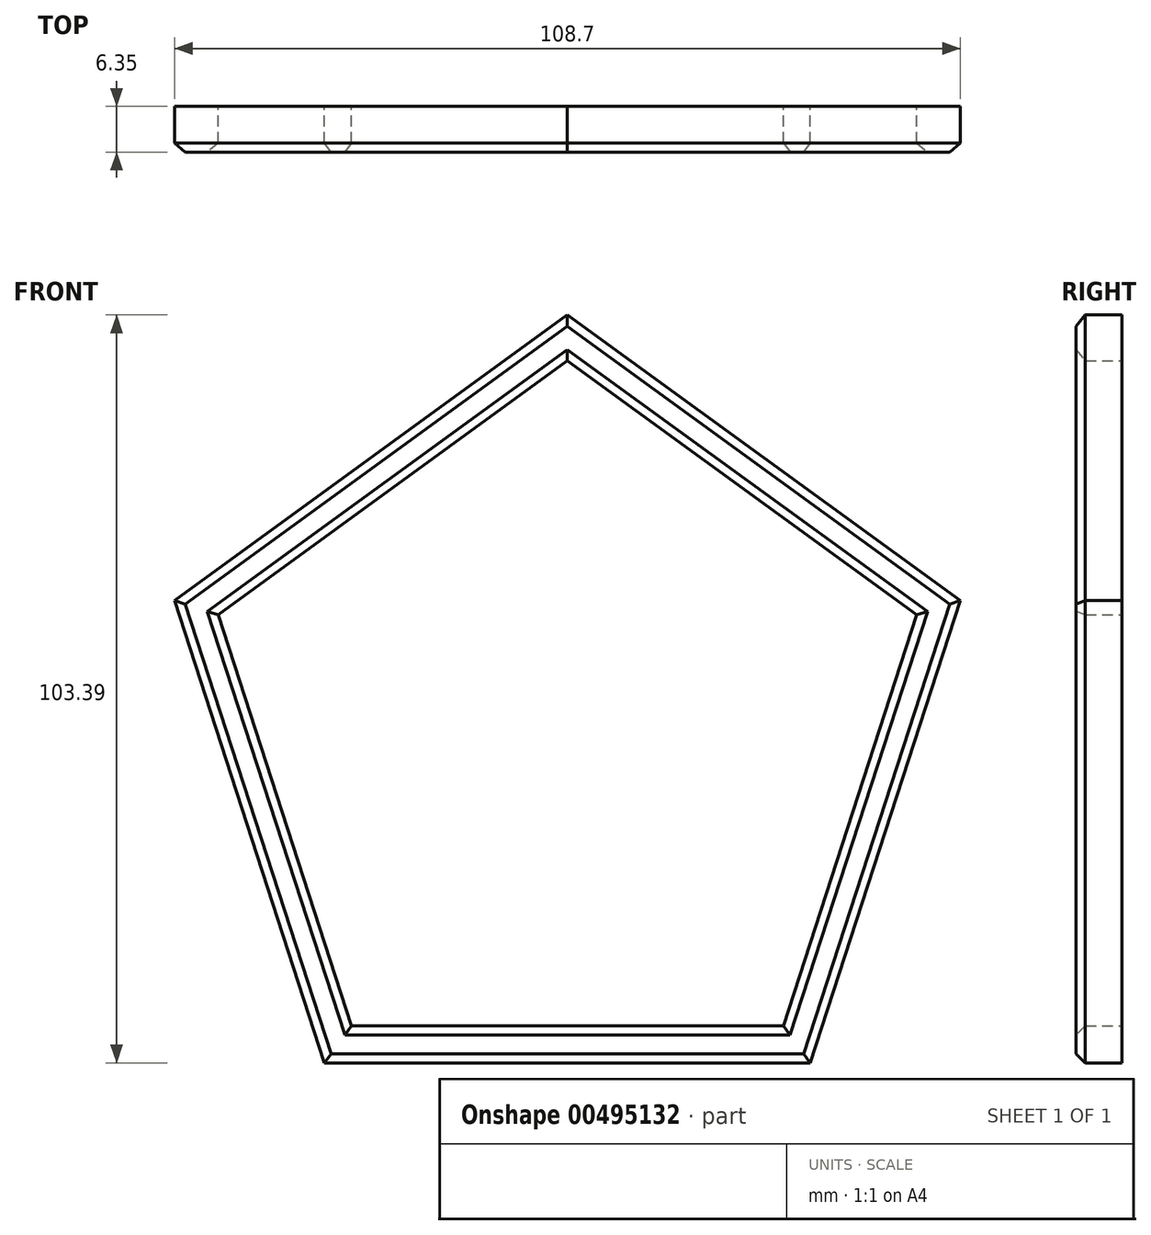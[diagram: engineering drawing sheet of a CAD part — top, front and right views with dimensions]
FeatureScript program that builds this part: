
annotation { "Feature Type Name" : "Feature", "Feature Type Description" : "" }
export const myFeature = defineFeature(function(context is Context, id is Id, definition is map)
    precondition{}
    {
        {
            var Q0;
            Q0=qCreatedBy(makeId("Front.planeOp"),FACE);
            var sketch = newSketch(context, id + "F0", { "sketchPlane" : qUnion([Q0])});
            skCircle(sketch, "E0.cCircle", {"center": v(0, 0) * mm, "radius": 50.8 * mm, "construction": true});
            skLineSegment(sketch, "E0.0", {"start": v(0, 50.8) * mm, "end": v(48.31, 15.7) * mm});
            skLineSegment(sketch, "E0.1", {"start": v(48.31, 15.7) * mm, "end": v(29.86, -41.1) * mm});
            skLineSegment(sketch, "E0.2", {"start": v(29.86, -41.1) * mm, "end": v(-29.86, -41.1) * mm});
            skLineSegment(sketch, "E0.3", {"start": v(-29.86, -41.1) * mm, "end": v(-48.31, 15.7) * mm});
            skLineSegment(sketch, "E0.4", {"start": v(-48.31, 15.7) * mm, "end": v(0, 50.8) * mm});
            skCircle(sketch, "E1.cCircle", {"center": v(0, 0) * mm, "radius": 57.15 * mm, "construction": true});
            skLineSegment(sketch, "E1.0", {"start": v(0, 57.15) * mm, "end": v(54.35, 17.66) * mm});
            skLineSegment(sketch, "E1.1", {"start": v(54.35, 17.66) * mm, "end": v(33.6, -46.24) * mm});
            skLineSegment(sketch, "E1.2", {"start": v(33.6, -46.24) * mm, "end": v(-33.6, -46.24) * mm});
            skLineSegment(sketch, "E1.3", {"start": v(-33.6, -46.24) * mm, "end": v(-54.35, 17.66) * mm});
            skLineSegment(sketch, "E1.4", {"start": v(-54.35, 17.66) * mm, "end": v(0, 57.15) * mm});
            skSolve(sketch);
        }
        {
            var Q0;
            Q0 = qSketchRegion(id + "F0", true);
            extrude(context, id + "F1", {"entities" : qUnion([Q0]), "depth" : 6.35 * mm});
        }
        {
            var Q0;
            Q0=makeQuery(id+"F1.opExtrude","CAP_FACE",FACE,{"disambiguationData":[OSD([sQuery(id+"F0.wireOp",EDGE,"E0.0"),sQuery(id+"F0.wireOp",EDGE,"E0.1"),sQuery(id+"F0.wireOp",EDGE,"E0.2"),sQuery(id+"F0.wireOp",EDGE,"E0.3"),sQuery(id+"F0.wireOp",EDGE,"E0.4"),sQuery(id+"F0.wireOp",EDGE,"E1.0"),sQuery(id+"F0.wireOp",EDGE,"E1.1"),sQuery(id+"F0.wireOp",EDGE,"E1.2"),sQuery(id+"F0.wireOp",EDGE,"E1.3"),sQuery(id+"F0.wireOp",EDGE,"E1.4")])],"isStart":false});
            chamfer(context, id + "F2", {"entities" : qUnion([Q0]), "chamferType" : ChamferType.OFFSET_ANGLE, "width" : 1.27 * mm, "oppositeDirection" : false, "angle" : 45 * degree, "tangentPropagation" : true});
        }
    });
